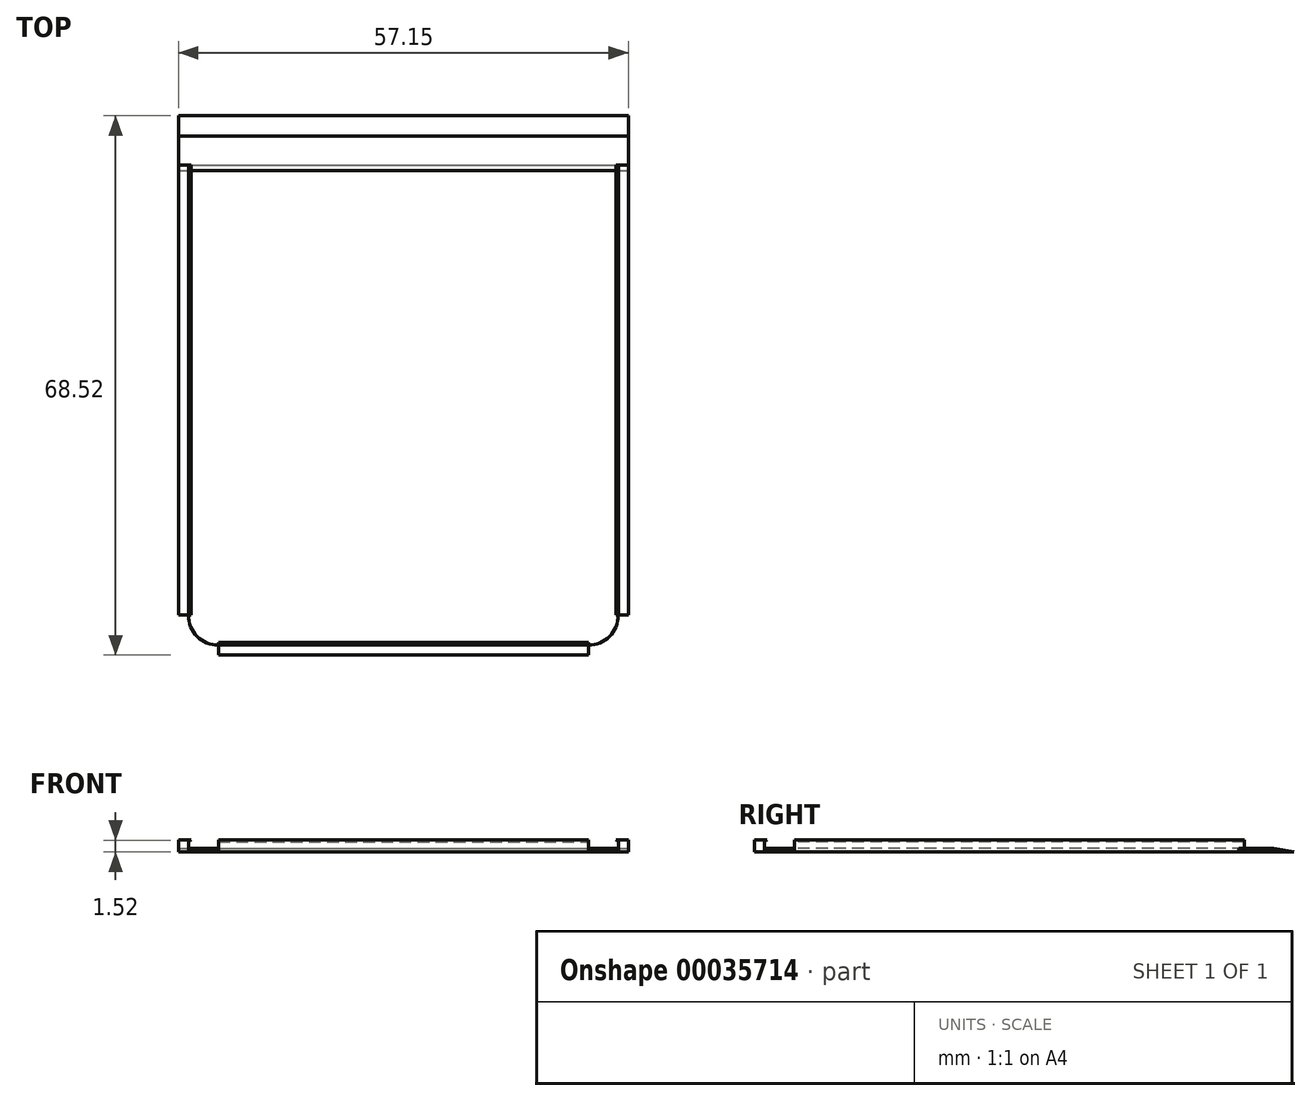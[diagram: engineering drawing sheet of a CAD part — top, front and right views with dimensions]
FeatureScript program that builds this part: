
annotation { "Feature Type Name" : "Feature", "Feature Type Description" : "" }
export const myFeature = defineFeature(function(context is Context, id is Id, definition is map)
    precondition{}
    {
        {
            var Q0;
            Q0=qCreatedBy(makeId("Top.planeOp"),FACE);
            var sketch = newSketch(context, id + "F0", { "sketchPlane" : qUnion([Q0])});
            skLineSegment(sketch, "E0.rect.bottom", {"start": v(-27.3, 30.48) * mm, "end": v(27.3, 30.48) * mm});
            skLineSegment(sketch, "E0.rect.top", {"start": v(-23.5, -30.48) * mm, "end": v(23.5, -30.48) * mm});
            skLineSegment(sketch, "E0.rect.left", {"start": v(-27.3, 30.48) * mm, "end": v(-27.3, -26.67) * mm});
            skLineSegment(sketch, "E0.rect.right", {"start": v(27.3, 30.48) * mm, "end": v(27.3, -26.67) * mm});
            skPoint(sketch, "E0.rect.middle", {"position": v(0, 0) * mm});
            skLineSegment(sketch, "E1.0", {"start": v(28.57, 30.48) * mm, "end": v(28.57, -26.67) * mm});
            skLineSegment(sketch, "E1.1", {"start": v(-23.5, -31.75) * mm, "end": v(23.5, -31.75) * mm});
            skLineSegment(sketch, "E1.2", {"start": v(-28.57, 30.48) * mm, "end": v(-28.57, -26.67) * mm});
            skLineSegment(sketch, "E2", {"start": v(27.3, 30.48) * mm, "end": v(28.57, 30.48) * mm});
            skLineSegment(sketch, "E3", {"start": v(-28.57, 30.48) * mm, "end": v(-27.3, 30.48) * mm});
            skLineSegment(sketch, "E4", {"start": v(0, -30.48) * mm, "end": v(0, -26.67) * mm, "construction": true});
            skLineSegment(sketch, "E5", {"start": v(0, -26.67) * mm, "end": v(-28.57, -26.67) * mm, "construction": true});
            skLineSegment(sketch, "E6", {"start": v(0, -26.67) * mm, "end": v(28.57, -26.67) * mm, "construction": true});
            skLineSegment(sketch, "E7", {"start": v(-27.3, 0) * mm, "end": v(-23.5, 0) * mm, "construction": true});
            skLineSegment(sketch, "E8", {"start": v(27.3, 0) * mm, "end": v(23.5, 0) * mm, "construction": true});
            skLineSegment(sketch, "E9", {"start": v(-23.5, 0) * mm, "end": v(-23.5, -31.75) * mm, "construction": true});
            skLineSegment(sketch, "E10", {"start": v(23.5, 0) * mm, "end": v(23.5, -31.75) * mm, "construction": true});
            skLineSegment(sketch, "E11", {"start": v(-28.57, -26.67) * mm, "end": v(-27.3, -26.67) * mm});
            skLineSegment(sketch, "E12", {"start": v(28.57, -26.67) * mm, "end": v(27.3, -26.67) * mm});
            skLineSegment(sketch, "E13", {"start": v(-23.5, -31.75) * mm, "end": v(-23.5, -30.48) * mm});
            skLineSegment(sketch, "E14", {"start": v(23.5, -31.75) * mm, "end": v(23.5, -30.48) * mm});
            skPoint(sketch, "E15.orphan", {"position": v(27.3, -30.48) * mm});
            skPoint(sketch, "E16.orphan", {"position": v(-27.3, -30.48) * mm});
            skArc(sketch, "E17", {"start": v(23.5, -30.48) * mm, "mid": v(26.19, -29.36) * mm, "end": v(27.3, -26.67) * mm});
            skArc(sketch, "E18", {"start": v(-27.3, -26.67) * mm, "mid": v(-26.19, -29.36) * mm, "end": v(-23.5, -30.48) * mm});
            skLineSegment(sketch, "E19.bottom", {"start": v(-27.3, 30.48) * mm, "end": v(26.06, 30.48) * mm});
            skSolve(sketch);
        }
        {
            var Q0;
            Q0=makeQuery(id+"F0.imprint","IMPRINT",FACE,{"disambiguationData":[TD([[makeQuery(id+"F0.imprint","IMPRINT",EDGE,{"derivedFrom":sQuery(id+"F0.wireOp",EDGE,"E0.rect.bottom")}),-1.0]])]});
            extrude(context, id + "F1", {"entities" : qUnion([Q0]), "depth" : 0.44 * mm});
        }
        {
            var Q0;
            Q0=makeQuery(id+"F0.imprint","IMPRINT",FACE,{"disambiguationData":[TD([[makeQuery(id+"F0.imprint","IMPRINT",EDGE,{"derivedFrom":sQuery(id+"F0.wireOp",EDGE,"E0.rect.left")}),-1.0]])]});
            var Q1;
            Q1=makeQuery(id+"F0.imprint","IMPRINT",FACE,{"disambiguationData":[TD([[makeQuery(id+"F0.imprint","IMPRINT",EDGE,{"derivedFrom":sQuery(id+"F0.wireOp",EDGE,"E0.rect.right")}),1.0]])]});
            var Q2;
            Q2=makeQuery(id+"F0.imprint","IMPRINT",FACE,{"disambiguationData":[TD([[makeQuery(id+"F0.imprint","IMPRINT",EDGE,{"derivedFrom":sQuery(id+"F0.wireOp",EDGE,"E0.rect.top")}),-1.0]])]});
            extrude(context, id + "F2", {"entities" : qUnion([Q0, Q1, Q2]), "operationType" : NewBodyOperationType.ADD, "depth" : 1.52 * mm});
        }
        {
            var Q0;
            Q0=makeQuery(id+"F2.opExtrude","SWEPT_FACE",FACE,{"disambiguationData":[OSD([sQuery(id+"F0.wireOp",EDGE,"E12")])]});
            var sketch = newSketch(context, id + "F3", { "sketchPlane" : qUnion([Q0])});
            skLineSegment(sketch, "E20", {"start": v(27.3, 1.52) * mm, "end": v(26.99, 1.52) * mm});
            skLineSegment(sketch, "E21", {"start": v(26.99, 1.52) * mm, "end": v(27.3, 1.27) * mm});
            skLineSegment(sketch, "E22", {"start": v(27.3, 1.52) * mm, "end": v(27.3, 1.27) * mm});
            skSolve(sketch);
        }
        {
            var Q0;
            Q0=makeQuery(id+"F3.imprint","IMPRINT",FACE,{"disambiguationData":[TD([[makeQuery(id+"F3.imprint","IMPRINT",EDGE,{"derivedFrom":sQuery(id+"F3.wireOp",EDGE,"E20")}),1.0]])]});
            extrude(context, id + "F4", {"entities" : qUnion([Q0]), "oppositeDirection" : true, "depth" : 57.15 * mm});
        }
        {
            var Q0;
            Q0=makeQuery(id+"F2.opExtrude","SWEPT_FACE",FACE,{"disambiguationData":[OSD([sQuery(id+"F0.wireOp",EDGE,"E11")])]});
            var sketch = newSketch(context, id + "F5", { "sketchPlane" : qUnion([Q0])});
            skLineSegment(sketch, "E23", {"start": v(-27.3, 1.52) * mm, "end": v(-26.99, 1.52) * mm});
            skLineSegment(sketch, "E24", {"start": v(-26.99, 1.52) * mm, "end": v(-27.3, 1.27) * mm});
            skLineSegment(sketch, "E25", {"start": v(-27.3, 1.27) * mm, "end": v(-27.3, 1.52) * mm});
            skSolve(sketch);
        }
        {
            var Q0;
            Q0=makeQuery(id+"F5.imprint","IMPRINT",FACE,{"disambiguationData":[TD([[makeQuery(id+"F5.imprint","IMPRINT",EDGE,{"derivedFrom":sQuery(id+"F5.wireOp",EDGE,"E23")}),-1.0]])]});
            extrude(context, id + "F6", {"entities" : qUnion([Q0]), "oppositeDirection" : true, "depth" : 57.15 * mm});
        }
        {
            var Q0;
            Q0=makeQuery(id+"F2.opExtrude","SWEPT_FACE",FACE,{"disambiguationData":[OSD([sQuery(id+"F0.wireOp",EDGE,"E14")])]});
            var sketch = newSketch(context, id + "F7", { "sketchPlane" : qUnion([Q0])});
            skLineSegment(sketch, "E26", {"start": v(-30.48, 1.52) * mm, "end": v(-30.16, 1.52) * mm});
            skLineSegment(sketch, "E27", {"start": v(-30.16, 1.52) * mm, "end": v(-30.48, 1.27) * mm});
            skLineSegment(sketch, "E28", {"start": v(-30.48, 1.27) * mm, "end": v(-30.48, 1.52) * mm});
            skSolve(sketch);
        }
        {
            var Q0;
            Q0=makeQuery(id+"F7.imprint","IMPRINT",FACE,{"disambiguationData":[TD([[makeQuery(id+"F7.imprint","IMPRINT",EDGE,{"derivedFrom":sQuery(id+"F7.wireOp",EDGE,"E26")}),-1.0]])]});
            var Q1;
            Q1=makeQuery(id+"F2.opExtrude","SWEPT_FACE",FACE,{"disambiguationData":[OSD([sQuery(id+"F0.wireOp",EDGE,"E13")])]});
            extrude(context, id + "F8", {"entities" : qUnion([Q0]), "endBound" : BoundingType.UP_TO_SURFACE, "oppositeDirection" : true, "endBoundEntityFace" : qUnion([Q1]), "depth" : 54.6 * mm});
        }
        {
            var Q0;
            Q0=qCreatedBy(makeId("Top.planeOp"),FACE);
            var sketch = newSketch(context, id + "F9", { "sketchPlane" : qUnion([Q0])});
            skLineSegment(sketch, "E29.rect.bottom", {"start": v(-28.58, 36.77) * mm, "end": v(28.58, 36.77) * mm});
            skLineSegment(sketch, "E29.rect.left", {"start": v(-28.58, 36.77) * mm, "end": v(-28.58, 29.8) * mm});
            skLineSegment(sketch, "E29.rect.right", {"start": v(28.58, 36.77) * mm, "end": v(28.58, 29.8) * mm});
            skPoint(sketch, "E29.rect.middle", {"position": v(0, 0) * mm});
            skLineSegment(sketch, "E30", {"start": v(-28.58, 29.8) * mm, "end": v(28.58, 29.8) * mm});
            skPoint(sketch, "E29.rect.top.start.orphan", {"position": v(-28.58, -36.77) * mm});
            skPoint(sketch, "E31.orphan", {"position": v(28.58, -36.77) * mm});
            skSolve(sketch);
        }
        {
            var Q0;
            Q0=makeQuery(id+"F9.imprint","IMPRINT",FACE,{"disambiguationData":[TD([[makeQuery(id+"F9.imprint","IMPRINT",EDGE,{"derivedFrom":sQuery(id+"F9.wireOp",EDGE,"E29.rect.bottom")}),-1.0]])]});
            extrude(context, id + "F10", {"entities" : qUnion([Q0]), "depth" : 0.46 * mm});
        }
        {
            var Q0;
            Q0=makeQuery(id+"F10.opExtrude","SWEPT_FACE",FACE,{"disambiguationData":[OSD([sQuery(id+"F9.wireOp",EDGE,"E29.rect.right")])]});
            var sketch = newSketch(context, id + "F11", { "sketchPlane" : qUnion([Q0])});
            skLineSegment(sketch, "E32", {"start": v(36.77, 0) * mm, "end": v(34.2, 0.46) * mm});
            skLineSegment(sketch, "E33", {"start": v(34.2, 0.46) * mm, "end": v(34.2, 0) * mm});
            skLineSegment(sketch, "E34", {"start": v(34.2, 0) * mm, "end": v(36.77, 0) * mm});
            skSolve(sketch);
        }
        {
            var Q0;
            {var subQ2=sQuery(id+"F11.wireOp",EDGE,"E32");Q0=makeQuery(id+"F11.imprint","IMPRINT",FACE,{"disambiguationData":[TD([[makeQuery(id+"F11.imprint","IMPRINT",EDGE,{"derivedFrom":subQ2}),-1.0]])]});}
            extrude(context, id + "F12", {"entities" : qUnion([Q0]), "operationType" : NewBodyOperationType.REMOVE, "oppositeDirection" : true, "depth" : 76.2 * mm});
        }
    });
